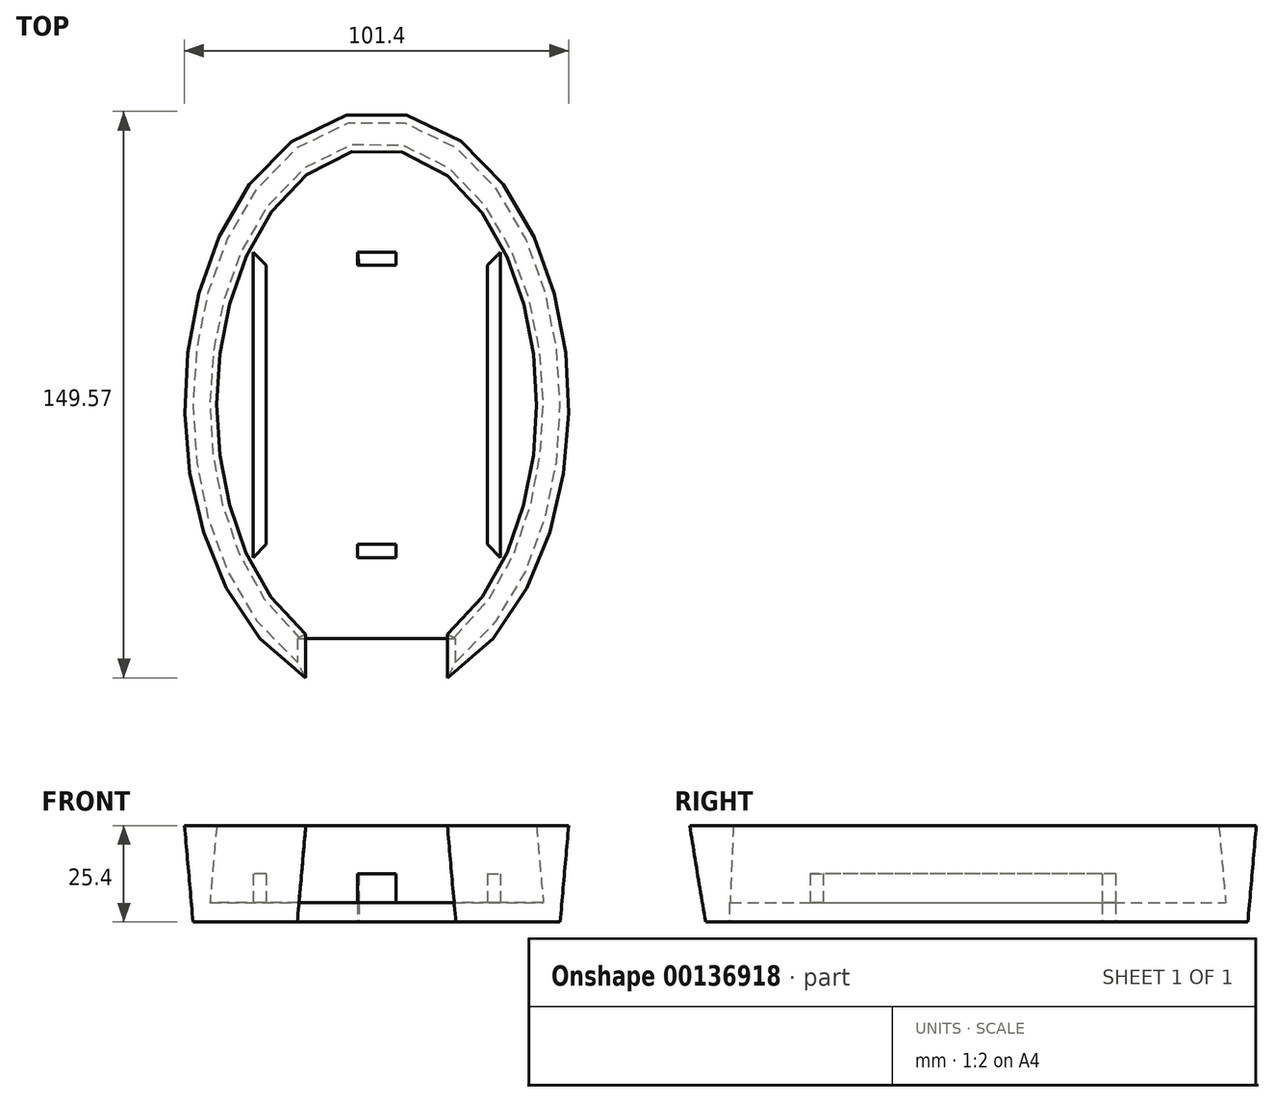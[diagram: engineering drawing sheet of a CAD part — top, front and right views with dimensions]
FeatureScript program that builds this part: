
annotation { "Feature Type Name" : "Feature", "Feature Type Description" : "" }
export const myFeature = defineFeature(function(context is Context, id is Id, definition is map)
    precondition{}
    {
        {
            var Q0;
            Q0=qCreatedBy(makeId("Top.planeOp"),FACE);
            var sketch = newSketch(context, id + "F0", { "sketchPlane" : qUnion([Q0])});
            skEllipticalArc(sketch, "E0", {});
            skLineSegment(sketch, "E1.bottom", {"start": v(5.08, 36.83) * mm, "end": v(-5.08, 36.83) * mm});
            skLineSegment(sketch, "E1.top", {"start": v(5.08, -36.83) * mm, "end": v(-5.08, -36.83) * mm});
            skLineSegment(sketch, "E1.left", {"start": v(29.21, 36.83) * mm, "end": v(29.2, -36.83) * mm});
            skLineSegment(sketch, "E1.right", {"start": v(-29.2, 36.83) * mm, "end": v(-29.21, -36.83) * mm});
            skEllipticalArc(sketch, "E2", {});
            skLineSegment(sketch, "E3", {"start": v(-20.92, -61.63) * mm, "end": v(-20.92, -67.9) * mm});
            skLineSegment(sketch, "E4", {"start": v(20.92, -61.63) * mm, "end": v(20.92, -67.9) * mm});
            skLineSegment(sketch, "E5", {"start": v(-20.92, -61.63) * mm, "end": v(20.92, -61.63) * mm});
            skLineSegment(sketch, "E6.bottom", {"start": v(5.08, 40.3) * mm, "end": v(-5.08, 40.3) * mm});
            skLineSegment(sketch, "E6.left", {"start": v(32.65, 40.3) * mm, "end": v(32.65, -40.3) * mm});
            skLineSegment(sketch, "E6.right", {"start": v(-32.65, 40.3) * mm, "end": v(-32.65, -40.3) * mm});
            skLineSegment(sketch, "E7", {"start": v(-5.08, -36.83) * mm, "end": v(-5.08, -40.3) * mm});
            skLineSegment(sketch, "E8", {"start": v(5.08, -40.3) * mm, "end": v(5.08, -36.83) * mm});
            skLineSegment(sketch, "E9", {"start": v(-5.08, -40.3) * mm, "end": v(5.08, -40.3) * mm});
            skLineSegment(sketch, "E10.trimOffspring", {"start": v(5.08, -40.3) * mm, "end": v(-5.08, -40.3) * mm});
            skPoint(sketch, "E11.end.orphan", {"position": v(0, -40.3) * mm});
            skLineSegment(sketch, "E12", {"start": v(-5.08, 36.83) * mm, "end": v(-5.08, 40.3) * mm});
            skLineSegment(sketch, "E13", {"start": v(-5.08, 40.3) * mm, "end": v(-4.62, 36.83) * mm});
            skLineSegment(sketch, "E14", {"start": v(5.08, 36.83) * mm, "end": v(5.08, 40.3) * mm});
            skLineSegment(sketch, "E15", {"start": v(-29.2, 36.83) * mm, "end": v(-32.65, 40.3) * mm});
            skLineSegment(sketch, "E16", {"start": v(29.21, 36.83) * mm, "end": v(32.65, 40.3) * mm});
            skLineSegment(sketch, "E17", {"start": v(29.2, -36.83) * mm, "end": v(32.65, -40.3) * mm});
            skLineSegment(sketch, "E18", {"start": v(-32.65, -40.3) * mm, "end": v(-29.21, -36.83) * mm});
            skPoint(sketch, "E19.end.orphan", {"position": v(29.2, -40.3) * mm});
            const initialGuessF0  = {"E0": [0, 0, 0, 1, 0.06985, 0.04445, 3.631549703945596, 2.6516356032339887], "E2": [0, 0, 0, 1, 0.0752761291176138, 0.04847984238359298, 3.5877151621904364, 2.6954701449891485]};
            skSetInitialGuess(sketch, initialGuessF0);
            skSolve(sketch);
        }
        {
            var Q0;
            Q0=makeQuery(id+"F0.imprint","IMPRINT",FACE,{"disambiguationData":[TD([[makeQuery(id+"F0.imprint","IMPRINT",EDGE,{"derivedFrom":sQuery(id+"F0.wireOp",EDGE,"E0")}),-1.0]])]});
            extrude(context, id + "F1", {"entities" : qUnion([Q0]), "depth" : 25.4 * mm, "hasDraft" : true, "draftAngle" : 5 * degree});
        }
        {
            var Q0;
            Q0=makeQuery(id+"F0.imprint","IMPRINT",FACE,{"disambiguationData":[TD([[makeQuery(id+"F0.imprint","IMPRINT",EDGE,{"derivedFrom":sQuery(id+"F0.wireOp",EDGE,"E0")}),1.0]])]});
            var Q1;
            Q1=makeQuery(id+"F0.imprint","IMPRINT",FACE,{"disambiguationData":[TD([[makeQuery(id+"F0.imprint","IMPRINT",EDGE,{"derivedFrom":sQuery(id+"F0.wireOp",EDGE,"E1.left")}),1.0]])]});
            var Q2;
            Q2=makeQuery(id+"F0.imprint","IMPRINT",FACE,{"disambiguationData":[TD([[makeQuery(id+"F0.imprint","IMPRINT",EDGE,{"derivedFrom":sQuery(id+"F0.wireOp",EDGE,"E1.top")}),1.0]])]});
            var Q3;
            Q3=makeQuery(id+"F0.imprint","IMPRINT",FACE,{"disambiguationData":[TD([[makeQuery(id+"F0.imprint","IMPRINT",EDGE,{"derivedFrom":sQuery(id+"F0.wireOp",EDGE,"E1.right")}),-1.0]])]});
            var Q4;
            Q4=makeQuery(id+"F0.imprint","IMPRINT",FACE,{"disambiguationData":[TD([[makeQuery(id+"F0.imprint","IMPRINT",EDGE,{"derivedFrom":sQuery(id+"F0.wireOp",EDGE,"E6.bottom")}),1.0]])]});
            extrude(context, id + "F2", {"entities" : qUnion([Q0, Q1, Q2, Q3, Q4]), "operationType" : NewBodyOperationType.ADD, "depth" : 5.08 * mm});
        }
        {
            var Q0;
            Q0=makeQuery(id+"F0.imprint","IMPRINT",FACE,{"disambiguationData":[TD([[makeQuery(id+"F0.imprint","IMPRINT",EDGE,{"derivedFrom":sQuery(id+"F0.wireOp",EDGE,"E1.left")}),1.0]])]});
            var Q1;
            Q1=makeQuery(id+"F0.imprint","IMPRINT",FACE,{"disambiguationData":[TD([[makeQuery(id+"F0.imprint","IMPRINT",EDGE,{"derivedFrom":sQuery(id+"F0.wireOp",EDGE,"E1.top")}),1.0]])]});
            var Q2;
            Q2=makeQuery(id+"F0.imprint","IMPRINT",FACE,{"disambiguationData":[TD([[makeQuery(id+"F0.imprint","IMPRINT",EDGE,{"derivedFrom":sQuery(id+"F0.wireOp",EDGE,"E1.right")}),-1.0]])]});
            var Q3;
            Q3=makeQuery(id+"F0.imprint","IMPRINT",FACE,{"disambiguationData":[TD([[makeQuery(id+"F0.imprint","IMPRINT",EDGE,{"derivedFrom":sQuery(id+"F0.wireOp",EDGE,"E6.bottom")}),1.0]])]});
            extrude(context, id + "F3", {"entities" : qUnion([Q0, Q1, Q2, Q3]), "operationType" : NewBodyOperationType.ADD, "depth" : 12.7 * mm});
        }
    });
